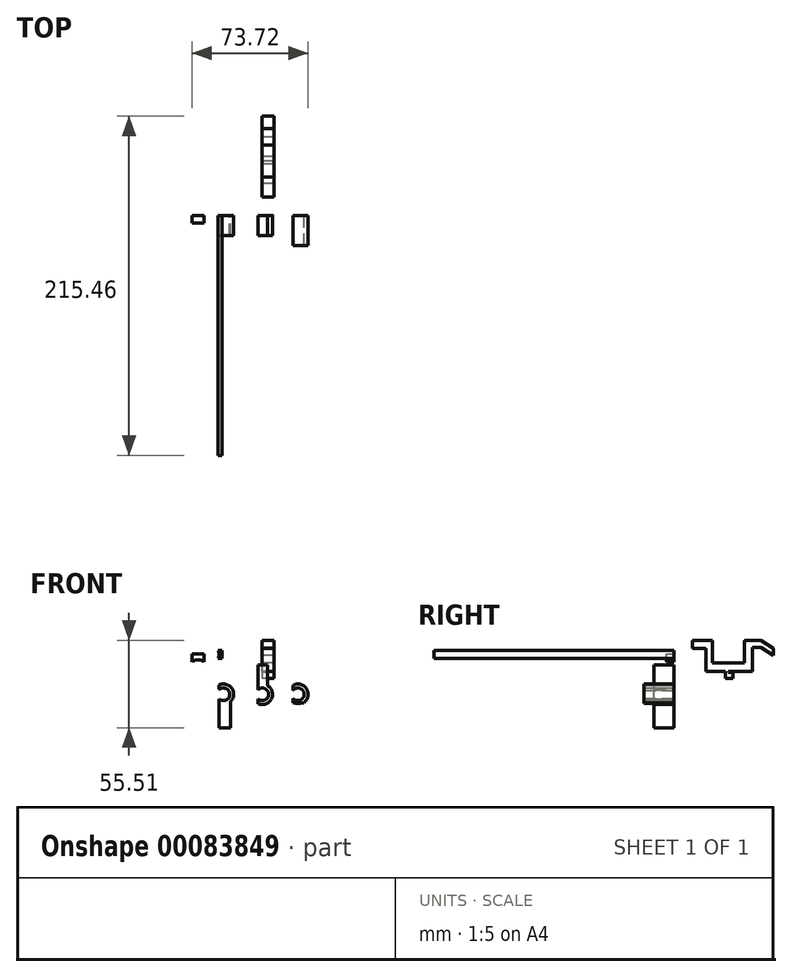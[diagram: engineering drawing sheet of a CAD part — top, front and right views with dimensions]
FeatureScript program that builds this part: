
annotation { "Feature Type Name" : "Feature", "Feature Type Description" : "" }
export const myFeature = defineFeature(function(context is Context, id is Id, definition is map)
    precondition{}
    {
        {
            var Q0;
            Q0=qCreatedBy(makeId("Front.planeOp"),FACE);
            var sketch = newSketch(context, id + "F0", { "sketchPlane" : qUnion([Q0])});
            skArc(sketch, "E0", {"start": v(-2.77, -2.89) * mm, "mid": v(4, 0) * mm, "end": v(-2.77, 2.89) * mm});
            skArc(sketch, "E1", {"start": v(-2.77, -5.92) * mm, "mid": v(5.74, -3.14) * mm, "end": v(3.5, 5.53) * mm});
            skLineSegment(sketch, "E2", {"start": v(-2.77, 5.92) * mm, "end": v(-2.77, 2.89) * mm});
            skLineSegment(sketch, "E3", {"start": v(-2.77, -2.89) * mm, "end": v(-2.77, -5.92) * mm});
            skLineSegment(sketch, "E4", {"start": v(-2.77, 5.92) * mm, "end": v(-2.77, 18.62) * mm});
            skLineSegment(sketch, "E5", {"start": v(-2.77, 18.62) * mm, "end": v(3.5, 18.62) * mm});
            skLineSegment(sketch, "E6", {"start": v(3.5, 18.62) * mm, "end": v(3.5, 5.53) * mm});
            skSolve(sketch);
        }
        {
            var Q0;
            Q0=qCreatedBy(makeId("Front.planeOp"),FACE);
            var sketch = newSketch(context, id + "F1", { "sketchPlane" : qUnion([Q0])});
            skArc(sketch, "E7", {"start": v(-27.29, -3) * mm, "mid": v(-20.63, 0) * mm, "end": v(-27.29, 3) * mm});
            skArc(sketch, "E8", {"start": v(-20.11, -4.73) * mm, "mid": v(-19.2, 3.64) * mm, "end": v(-27.29, 5.98) * mm});
            skLineSegment(sketch, "E9", {"start": v(-27.29, 5.98) * mm, "end": v(-27.29, 3) * mm});
            skLineSegment(sketch, "E10", {"start": v(-27.29, -3) * mm, "end": v(-27.29, -5.98) * mm});
            skLineSegment(sketch, "E11", {"start": v(-27.29, -5.98) * mm, "end": v(-27.29, -21.22) * mm});
            skLineSegment(sketch, "E12", {"start": v(-27.29, -21.22) * mm, "end": v(-20.11, -21.22) * mm});
            skLineSegment(sketch, "E13", {"start": v(-20.11, -21.22) * mm, "end": v(-20.11, -4.73) * mm});
            skSolve(sketch);
        }
        {
            var Q0;
            Q0=qCreatedBy(makeId("Front.planeOp"),FACE);
            var sketch = newSketch(context, id + "F2", { "sketchPlane" : qUnion([Q0])});
            skArc(sketch, "E14", {"start": v(19.46, -2.45) * mm, "mid": v(26.62, 0) * mm, "end": v(19.46, 2.45) * mm});
            skArc(sketch, "E15", {"start": v(26.46, -5.3) * mm, "mid": v(28.14, 3.5) * mm, "end": v(19.46, 5.72) * mm});
            skArc(sketch, "E16", {"start": v(30.68, -3.9) * mm, "mid": v(22.89, -5.68) * mm, "end": v(15.05, -4.12) * mm});
            skArc(sketch, "E17", {"start": v(30.68, -5.66) * mm, "mid": v(22.88, -7.29) * mm, "end": v(15.05, -5.85) * mm});
            skLineSegment(sketch, "E18", {"start": v(15.05, -4.12) * mm, "end": v(15.05, -5.85) * mm});
            skLineSegment(sketch, "E19", {"start": v(30.68, -3.9) * mm, "end": v(30.68, -5.66) * mm});
            skLineSegment(sketch, "E20", {"start": v(19.46, -2.45) * mm, "end": v(19.46, -5.42) * mm});
            skLineSegment(sketch, "E21", {"start": v(19.46, 2.45) * mm, "end": v(19.46, 5.72) * mm});
            skPoint(sketch, "E22.orphan", {"position": v(18.84, 1.3) * mm});
            skPoint(sketch, "E23.start.orphan", {"position": v(18.84, -1.3) * mm});
            skSolve(sketch);
        }
        {
            var Q0;
            Q0=makeQuery(id+"F1.imprint","IMPRINT",FACE,{"disambiguationData":[TD([[makeQuery(id+"F1.imprint","IMPRINT",EDGE,{"derivedFrom":sQuery(id+"F1.wireOp",EDGE,"E7")}),-1.0]])]});
            extrude(context, id + "F3", {"entities" : qUnion([Q0]), "depth" : 12.7 * mm});
        }
        {
            var Q0;
            Q0=makeQuery(id+"F0.imprint","IMPRINT",FACE,{"disambiguationData":[TD([[makeQuery(id+"F0.imprint","IMPRINT",EDGE,{"derivedFrom":sQuery(id+"F0.wireOp",EDGE,"E0")}),-1.0]])]});
            extrude(context, id + "F4", {"entities" : qUnion([Q0]), "depth" : 12.7 * mm});
        }
        {
            var Q0;
            Q0=makeQuery(id+"F2.imprint","IMPRINT",FACE,{"disambiguationData":[TD([[makeQuery(id+"F2.imprint","IMPRINT",EDGE,{"derivedFrom":sQuery(id+"F2.wireOp",EDGE,"E14")}),-1.0]])]});
            var Q1;
            Q1=makeQuery(id+"F2.imprint","IMPRINT",FACE,{"disambiguationData":[TD([[makeQuery(id+"F2.imprint","IMPRINT",EDGE,{"derivedFrom":sQuery(id+"F2.wireOp",EDGE,"E17")}),-1.0]])]});
            extrude(context, id + "F5", {"entities" : qUnion([Q0, Q1]), "depth" : 19.05 * mm});
        }
        {
            var Q0;
            Q0=qCreatedBy(makeId("Front.planeOp"),FACE);
            var sketch = newSketch(context, id + "F6", { "sketchPlane" : qUnion([Q0])});
            skLineSegment(sketch, "E24.bottom", {"start": v(-28.03, 27.94) * mm, "end": v(-25.51, 27.94) * mm});
            skLineSegment(sketch, "E24.top", {"start": v(-28.03, 22.86) * mm, "end": v(-25.51, 22.86) * mm});
            skLineSegment(sketch, "E24.right", {"start": v(-25.51, 27.94) * mm, "end": v(-25.51, 22.86) * mm});
            skArc(sketch, "E25", {"start": v(-28.03, 22.86) * mm, "mid": v(-27.51, 25.4) * mm, "end": v(-28.03, 27.94) * mm});
            skPoint(sketch, "E25.centerSnap0", {"position": v(-29.32, 25.4) * mm});
            skPoint(sketch, "E26.orphan", {"position": v(-29.32, 22.86) * mm});
            skPoint(sketch, "E27.orphan", {"position": v(-29.32, 27.94) * mm});
            skSolve(sketch);
        }
        {
            var Q0;
            Q0=makeQuery(id+"F6.imprint","IMPRINT",FACE,{"disambiguationData":[TD([[makeQuery(id+"F6.imprint","IMPRINT",EDGE,{"derivedFrom":sQuery(id+"F6.wireOp",EDGE,"E24.bottom")}),-1.0]])]});
            extrude(context, id + "F7", {"entities" : qUnion([Q0]), "depth" : 152.4 * mm});
        }
        {
            var Q0;
            Q0=qCreatedBy(makeId("Right.planeOp"),FACE);
            var sketch = newSketch(context, id + "F8", { "sketchPlane" : qUnion([Q0])});
            skLineSegment(sketch, "E28.bottom", {"start": v(11.53, 34.3) * mm, "end": v(24.41, 34.3) * mm});
            skLineSegment(sketch, "E28.top", {"start": v(11.53, 29.2) * mm, "end": v(20.34, 29.2) * mm});
            skLineSegment(sketch, "E28.left", {"start": v(11.53, 34.3) * mm, "end": v(11.53, 29.2) * mm});
            skLineSegment(sketch, "E28.right", {"start": v(24.41, 34.3) * mm, "end": v(24.41, 29.2) * mm});
            skLineSegment(sketch, "E29.left", {"start": v(24.41, 29.2) * mm, "end": v(24.41, 20.05) * mm});
            skLineSegment(sketch, "E29.right", {"start": v(20.34, 29.2) * mm, "end": v(20.34, 20.05) * mm});
            skLineSegment(sketch, "E30.bottom", {"start": v(24.41, 20.05) * mm, "end": v(44.76, 20.05) * mm});
            skLineSegment(sketch, "E30.top", {"start": v(20.34, 14.63) * mm, "end": v(32.55, 14.63) * mm});
            skLineSegment(sketch, "E30.left", {"start": v(20.34, 20.05) * mm, "end": v(20.34, 14.63) * mm});
            skLineSegment(sketch, "E31.bottom", {"start": v(44.76, 14.63) * mm, "end": v(49.84, 14.63) * mm});
            skLineSegment(sketch, "E31.top", {"start": v(44.76, 34.3) * mm, "end": v(49.84, 34.3) * mm});
            skLineSegment(sketch, "E31.left", {"start": v(44.76, 20.05) * mm, "end": v(44.76, 34.3) * mm});
            skLineSegment(sketch, "E31.right", {"start": v(49.84, 14.63) * mm, "end": v(49.84, 29.88) * mm});
            skLineSegment(sketch, "E32.bottom", {"start": v(49.84, 34.3) * mm, "end": v(55.27, 34.3) * mm});
            skLineSegment(sketch, "E32.top", {"start": v(49.84, 29.88) * mm, "end": v(55.27, 29.88) * mm});
            skLineSegment(sketch, "E33", {"start": v(55.27, 34.3) * mm, "end": v(63.06, 29.2) * mm});
            skLineSegment(sketch, "E34", {"start": v(55.27, 29.88) * mm, "end": v(63.06, 24.8) * mm});
            skLineSegment(sketch, "E35", {"start": v(63.06, 29.2) * mm, "end": v(63.06, 24.8) * mm});
            skLineSegment(sketch, "E36.left", {"start": v(32.55, 14.63) * mm, "end": v(32.55, 10.21) * mm});
            skLineSegment(sketch, "E36.right", {"start": v(34.5, 14.63) * mm, "end": v(34.5, 13.84) * mm});
            skLineSegment(sketch, "E37.bottom", {"start": v(34.5, 13.84) * mm, "end": v(37.45, 13.84) * mm});
            skLineSegment(sketch, "E37.right", {"start": v(37.45, 13.84) * mm, "end": v(37.45, 10.21) * mm});
            skLineSegment(sketch, "E38.trimOffspring", {"start": v(34.5, 14.63) * mm, "end": v(44.76, 14.63) * mm});
            skPoint(sketch, "E39.trimOffspring.end.orphan", {"position": v(35, -2.45) * mm});
            skPoint(sketch, "E40.start.orphan", {"position": v(35, 10.68) * mm});
            skPoint(sketch, "E36.top.end.orphan", {"position": v(34.5, 9.07) * mm});
            skPoint(sketch, "E41.orphan", {"position": v(37.45, 9.07) * mm});
            skPoint(sketch, "E42.orphan", {"position": v(32.55, 10.68) * mm});
            skPoint(sketch, "E43.start.orphan", {"position": v(37.45, 10.68) * mm});
            skPoint(sketch, "E44.center.orphan", {"position": v(35, 4.12) * mm});
            skLineSegment(sketch, "E45", {"start": v(32.55, 10.21) * mm, "end": v(37.45, 10.21) * mm});
            skSolve(sketch);
        }
        {
            var Q0;
            Q0=makeQuery(id+"F8.imprint","IMPRINT",FACE,{"disambiguationData":[TD([[makeQuery(id+"F8.imprint","IMPRINT",EDGE,{"derivedFrom":sQuery(id+"F8.wireOp",EDGE,"E28.bottom")}),-1.0]])]});
            extrude(context, id + "F9", {"entities" : qUnion([Q0]), "depth" : 7.62 * mm});
        }
        {
            var Q0;
            Q0=qCreatedBy(makeId("Front.planeOp"),FACE);
            var sketch = newSketch(context, id + "F10", { "sketchPlane" : qUnion([Q0])});
            skLineSegment(sketch, "E46.top", {"start": v(-44.56, 25.5) * mm, "end": v(-36.94, 25.5) * mm});
            skLineSegment(sketch, "E46.left", {"start": v(-44.56, 20.67) * mm, "end": v(-44.56, 25.5) * mm});
            skLineSegment(sketch, "E46.right", {"start": v(-36.94, 20.67) * mm, "end": v(-36.94, 25.5) * mm});
            skArc(sketch, "E47", {"start": v(-36.94, 20.67) * mm, "mid": v(-40.75, 21.89) * mm, "end": v(-44.56, 20.67) * mm});
            skPoint(sketch, "E48.start.orphan", {"position": v(-40.75, 18.27) * mm});
            skPoint(sketch, "E49.orphan", {"position": v(-36.94, 18.27) * mm});
            skPoint(sketch, "E50.orphan", {"position": v(-44.56, 18.27) * mm});
            skPoint(sketch, "E51.orphan", {"position": v(-44.56, 21.89) * mm});
            skPoint(sketch, "E52.start.orphan", {"position": v(-36.94, 21.89) * mm});
            skSolve(sketch);
        }
        {
            var Q0;
            Q0=makeQuery(id+"F10.imprint","IMPRINT",FACE,{"disambiguationData":[TD([[makeQuery(id+"F10.imprint","IMPRINT",EDGE,{"derivedFrom":sQuery(id+"F10.wireOp",EDGE,"E46.top")}),-1.0]])]});
            extrude(context, id + "F11", {"entities" : qUnion([Q0]), "depth" : 4.9 * mm});
        }
    });
